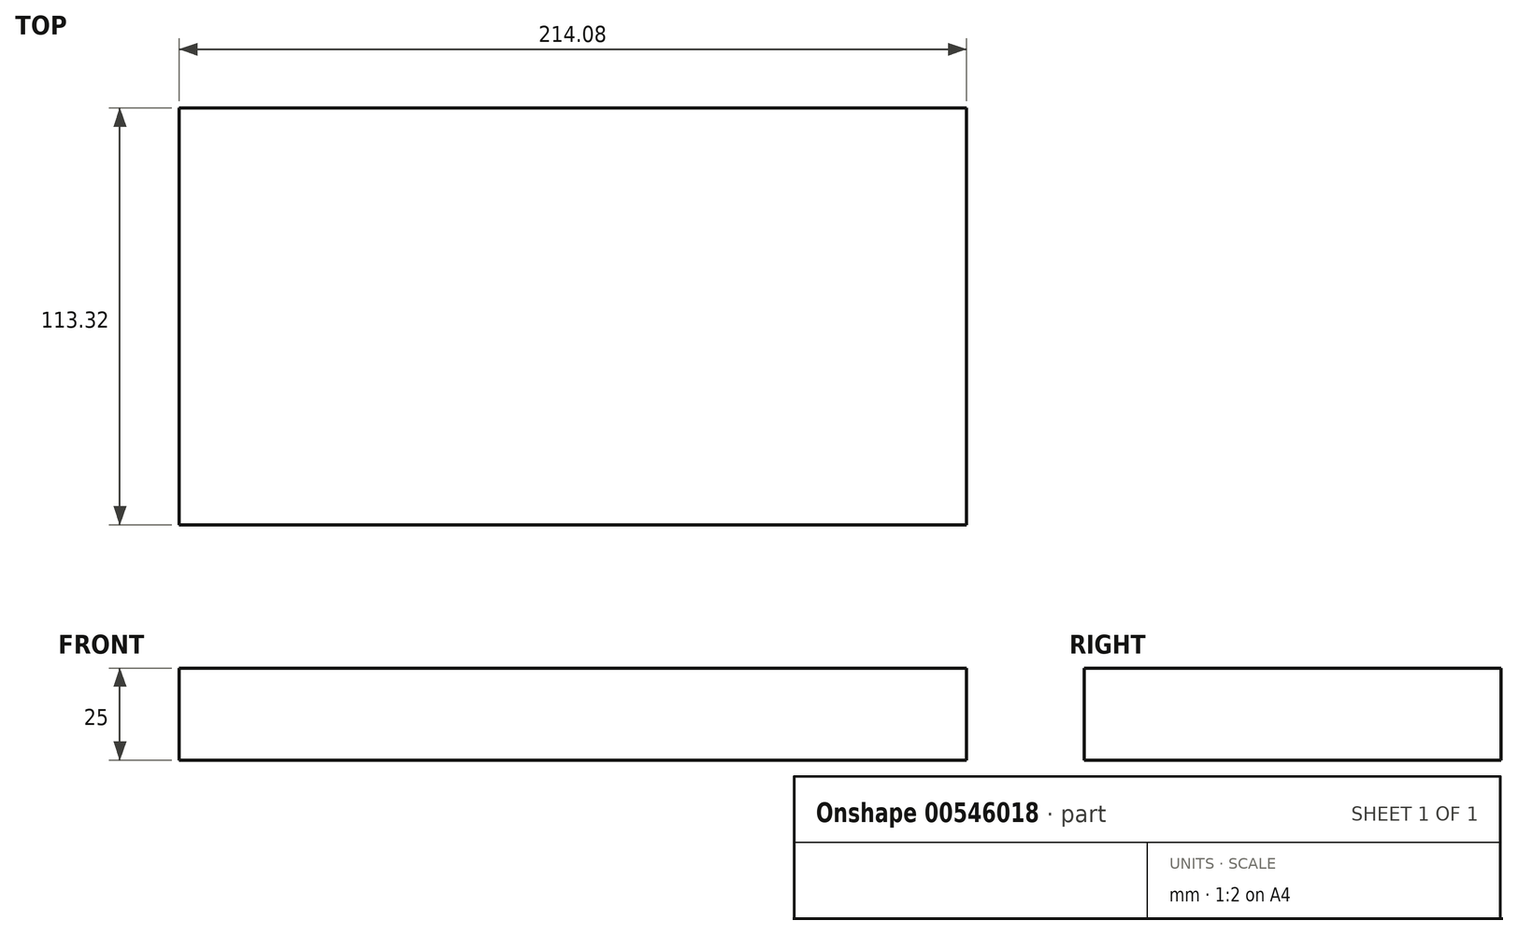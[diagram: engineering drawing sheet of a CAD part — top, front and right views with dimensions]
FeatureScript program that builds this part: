
annotation { "Feature Type Name" : "Feature", "Feature Type Description" : "" }
export const myFeature = defineFeature(function(context is Context, id is Id, definition is map)
    precondition{}
    {
        {
            var Q0;
            Q0=qCreatedBy(makeId("Top.planeOp"),FACE);
            var sketch = newSketch(context, id + "F0", { "sketchPlane" : qUnion([Q0])});
            skLineSegment(sketch, "E0.bottom", {"start": v(-107.04, 51.7) * mm, "end": v(107.04, 51.7) * mm});
            skLineSegment(sketch, "E0.top", {"start": v(-107.04, -61.62) * mm, "end": v(107.04, -61.62) * mm});
            skLineSegment(sketch, "E0.left", {"start": v(-107.04, 51.7) * mm, "end": v(-107.04, -61.62) * mm});
            skLineSegment(sketch, "E0.right", {"start": v(107.04, 51.7) * mm, "end": v(107.04, -61.62) * mm});
            skPoint(sketch, "E0.middle", {"position": v(0, -4.96) * mm});
            skSolve(sketch);
        }
        {
            var Q0;
            Q0=makeQuery(id+"F0.imprint","IMPRINT",FACE,{"disambiguationData":[TD([[makeQuery(id+"F0.imprint","IMPRINT",EDGE,{"derivedFrom":sQuery(id+"F0.wireOp",EDGE,"E0.bottom")}),-1.0]])]});
            extrude(context, id + "F1", {"entities" : qUnion([Q0]), "depth" : 25 * mm, "offsetDistance" : 25 * mm});
        }
    });
